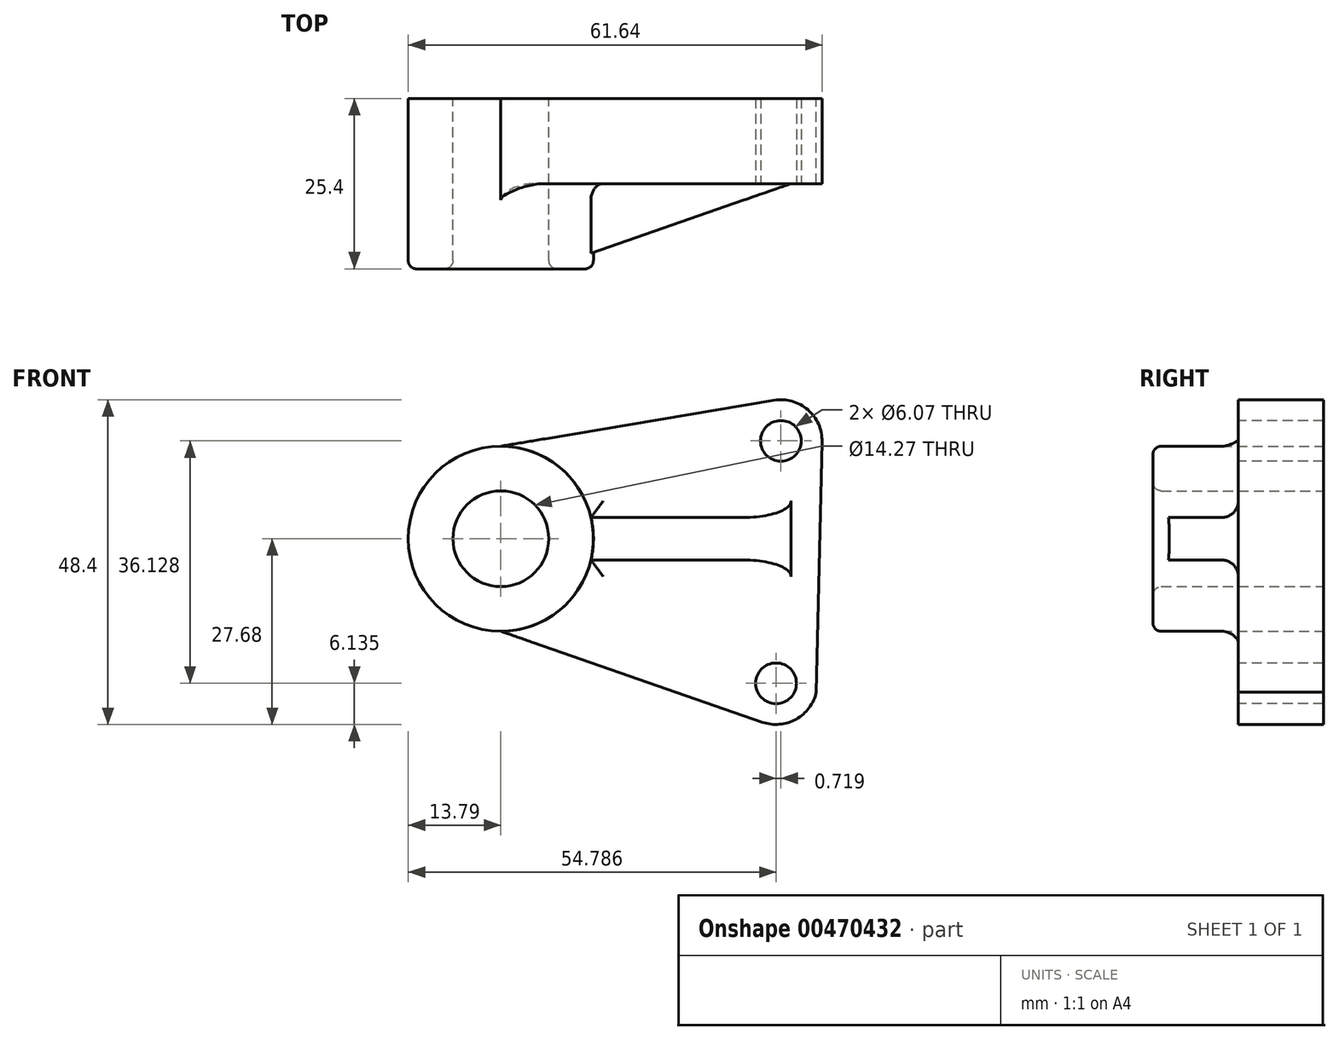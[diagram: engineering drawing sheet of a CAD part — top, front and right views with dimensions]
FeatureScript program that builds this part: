
annotation { "Feature Type Name" : "Feature", "Feature Type Description" : "" }
export const myFeature = defineFeature(function(context is Context, id is Id, definition is map)
    precondition{}
    {
        {
            var Q0;
            Q0=qCreatedBy(makeId("Front.planeOp"),FACE);
            var sketch = newSketch(context, id + "F0", { "sketchPlane" : qUnion([Q0])});
            skCircle(sketch, "E0", {"center": v(0, 0) * mm, "radius": 7.14 * mm});
            skCircle(sketch, "E1", {"center": v(0, 0) * mm, "radius": 13.79 * mm});
            skLineSegment(sketch, "E2", {"start": v(0, -13.79) * mm, "end": v(38.98, -27.34) * mm});
            skLineSegment(sketch, "E3", {"start": v(0, 13.79) * mm, "end": v(40.7, 20.63) * mm});
            skArc(sketch, "E4", {"start": v(40.7, 20.63) * mm, "mid": v(45.73, 19.22) * mm, "end": v(47.85, 14.44) * mm});
            skArc(sketch, "E5", {"start": v(38.98, -27.34) * mm, "mid": v(43.99, -26.9) * mm, "end": v(46.99, -22.87) * mm});
            skLineSegment(sketch, "E6", {"start": v(47.85, 14.44) * mm, "end": v(46.99, -22.87) * mm});
            skLineSegment(sketch, "E7", {"start": v(0, 0) * mm, "end": v(47.42, -1.1) * mm});
            skPoint(sketch, "E7.endSnap0", {"position": v(47.42, -4.21) * mm});
            skSolve(sketch);
        }
        {
            var Q0;
            Q0=qSketchRegion(id+"F0",true);
            extrude(context, id + "F1", {"entities" : qUnion([Q0]), "depth" : 12.7 * mm});
        }
        {
            var Q0;
            Q0=makeQuery(id+"F0.imprint","IMPRINT",FACE,{"disambiguationData":[TD([[makeQuery(id+"F0.imprint","IMPRINT",EDGE,{"derivedFrom":sQuery(id+"F0.wireOp",EDGE,"E0")}),-1.0]])]});
            extrude(context, id + "F2", {"entities" : qUnion([Q0]), "operationType" : NewBodyOperationType.ADD, "depth" : 25.4 * mm});
        }
        {
            var Q0;
            Q0=makeQuery(id+"F1.opExtrude","CAP_FACE",FACE,{"disambiguationData":[OSD([sQuery(id+"F0.wireOp",EDGE,"E0"),sQuery(id+"F0.wireOp",EDGE,"E1"),sQuery(id+"F0.wireOp",EDGE,"E2"),sQuery(id+"F0.wireOp",EDGE,"E3"),sQuery(id+"F0.wireOp",EDGE,"E4"),sQuery(id+"F0.wireOp",EDGE,"E5"),sQuery(id+"F0.wireOp",EDGE,"E6")])],"isStart":false});
            var sketch = newSketch(context, id + "F3", { "sketchPlane" : qUnion([Q0])});
            skCircle(sketch, "E8", {"center": v(41.72, 14.58) * mm, "radius": 3.03 * mm});
            skCircle(sketch, "E9", {"center": v(41, -21.54) * mm, "radius": 3.03 * mm});
            skSolve(sketch);
        }
        {
            var Q0;
            Q0=makeQuery(id+"F3.imprint","IMPRINT",FACE,{"disambiguationData":[TD([[makeQuery(id+"F3.imprint","IMPRINT",EDGE,{"derivedFrom":sQuery(id+"F3.wireOp",EDGE,"E9")}),1.0]])]});
            var Q1;
            Q1=makeQuery(id+"F3.imprint","IMPRINT",FACE,{"disambiguationData":[TD([[makeQuery(id+"F3.imprint","IMPRINT",EDGE,{"derivedFrom":sQuery(id+"F3.wireOp",EDGE,"E8")}),1.0]])]});
            extrude(context, id + "F4", {"entities" : qUnion([Q0, Q1]), "operationType" : NewBodyOperationType.REMOVE, "oppositeDirection" : true, "depth" : 25.4 * mm});
        }
        {
            var Q0;
            Q0=makeQuery(id+"F2.opExtrude","CAP_EDGE",EDGE,{"disambiguationData":[OSD([sQuery(id+"F0.wireOp",EDGE,"E1")])],"isStart":false});
            var Q1;
            Q1=makeQuery(id+"F2.opExtrude","CAP_EDGE",EDGE,{"disambiguationData":[OSD([sQuery(id+"F0.wireOp",EDGE,"E0")])],"isStart":false});
            fillet(context, id + "F5", {"entities" : qUnion([Q0, Q1]), "radius" : 1.23 * mm, "tangentPropagation" : true, "allowEdgeOverflow" : false});
        }
        {
            var Q0;
            Q0=qCreatedBy(makeId("Top.planeOp"),FACE);
            var sketch = newSketch(context, id + "F6", { "sketchPlane" : qUnion([Q0])});
            skLineSegment(sketch, "E10", {"start": v(13.33, -23.12) * mm, "end": v(44.47, -12.27) * mm});
            skLineSegment(sketch, "E11", {"start": v(44.47, -12.27) * mm, "end": v(13.33, -12.27) * mm});
            skLineSegment(sketch, "E12", {"start": v(13.33, -12.27) * mm, "end": v(13.33, -23.12) * mm});
            skSolve(sketch);
        }
        {
            var Q0;
            Q0=qSketchRegion(id+"F6",true);
            extrude(context, id + "F7", {"entities" : qUnion([Q0]), "operationType" : NewBodyOperationType.ADD, "depth" : 6.35 * mm, "symmetric" : true});
        }
        {
            var Q0;
            {var subQ0=sQuery(id+"F0.wireOp",EDGE,"E1");var subQ1=makeQuery(id+"F2.opExtrude","SWEPT_FACE",FACE,{"disambiguationData":[OSD([subQ0])]});var subQ2=sQuery(id+"F0.wireOp",EDGE,"E2");var subQ3=makeQuery(id+"F1.opExtrude","CAP_FACE",FACE,{"disambiguationData":[OSD([sQuery(id+"F0.wireOp",EDGE,"E0"),subQ0,subQ2,sQuery(id+"F0.wireOp",EDGE,"E3"),sQuery(id+"F0.wireOp",EDGE,"E4"),sQuery(id+"F0.wireOp",EDGE,"E5"),sQuery(id+"F0.wireOp",EDGE,"E6")])],"isStart":false});Q0=makeQuery(id+"F7.boolean.opBoolean","SPLIT",EDGE,{"disambiguationData":[TD([makeQuery(id+"F1.opExtrude","SWEPT_FACE",FACE,{"disambiguationData":[OSD([subQ2])]})])],"derivedFrom":makeQuery(id+"F2.boolean.opBoolean","INTERSECT",EDGE,{"derivedFrom":[subQ3,subQ1]})});}
            var Q1;
            Q1=makeQuery(id+"F7.boolean.opBoolean","INTERSECT",EDGE,{"derivedFrom":[makeQuery(id+"F1.opExtrude","CAP_FACE",FACE,{"disambiguationData":[OSD([sQuery(id+"F0.wireOp",EDGE,"E0"),sQuery(id+"F0.wireOp",EDGE,"E1"),sQuery(id+"F0.wireOp",EDGE,"E2"),sQuery(id+"F0.wireOp",EDGE,"E3"),sQuery(id+"F0.wireOp",EDGE,"E4"),sQuery(id+"F0.wireOp",EDGE,"E5"),sQuery(id+"F0.wireOp",EDGE,"E6")])],"isStart":false}),makeQuery(id+"F7.opExtrude","CAP_FACE",FACE,{"disambiguationData":[OSD([sQuery(id+"F6.wireOp",EDGE,"E10"),sQuery(id+"F6.wireOp",EDGE,"E11"),sQuery(id+"F6.wireOp",EDGE,"E12")])],"isStart":true})]});
            var Q2;
            {var subQ0=sQuery(id+"F0.wireOp",EDGE,"E1");var subQ1=makeQuery(id+"F2.opExtrude","SWEPT_FACE",FACE,{"disambiguationData":[OSD([subQ0])]});var subQ2=sQuery(id+"F0.wireOp",EDGE,"E3");var subQ3=makeQuery(id+"F1.opExtrude","CAP_FACE",FACE,{"disambiguationData":[OSD([sQuery(id+"F0.wireOp",EDGE,"E0"),subQ0,sQuery(id+"F0.wireOp",EDGE,"E2"),subQ2,sQuery(id+"F0.wireOp",EDGE,"E4"),sQuery(id+"F0.wireOp",EDGE,"E5"),sQuery(id+"F0.wireOp",EDGE,"E6")])],"isStart":false});Q2=makeQuery(id+"F7.boolean.opBoolean","SPLIT",EDGE,{"disambiguationData":[TD([makeQuery(id+"F1.opExtrude","SWEPT_FACE",FACE,{"disambiguationData":[OSD([subQ2])]})])],"derivedFrom":makeQuery(id+"F2.boolean.opBoolean","INTERSECT",EDGE,{"derivedFrom":[subQ3,subQ1]})});}
            var Q3;
            Q3=makeQuery(id+"F7.boolean.opBoolean","INTERSECT",EDGE,{"derivedFrom":[makeQuery(id+"F1.opExtrude","CAP_FACE",FACE,{"disambiguationData":[OSD([sQuery(id+"F0.wireOp",EDGE,"E0"),sQuery(id+"F0.wireOp",EDGE,"E1"),sQuery(id+"F0.wireOp",EDGE,"E2"),sQuery(id+"F0.wireOp",EDGE,"E3"),sQuery(id+"F0.wireOp",EDGE,"E4"),sQuery(id+"F0.wireOp",EDGE,"E5"),sQuery(id+"F0.wireOp",EDGE,"E6")])],"isStart":false}),makeQuery(id+"F7.opExtrude","CAP_FACE",FACE,{"disambiguationData":[OSD([sQuery(id+"F6.wireOp",EDGE,"E10"),sQuery(id+"F6.wireOp",EDGE,"E11"),sQuery(id+"F6.wireOp",EDGE,"E12")])],"isStart":false})]});
            fillet(context, id + "F8", {"entities" : qUnion([Q0, Q1, Q2, Q3]), "radius" : 2.45 * mm, "tangentPropagation" : true, "allowEdgeOverflow" : false});
        }
    });
